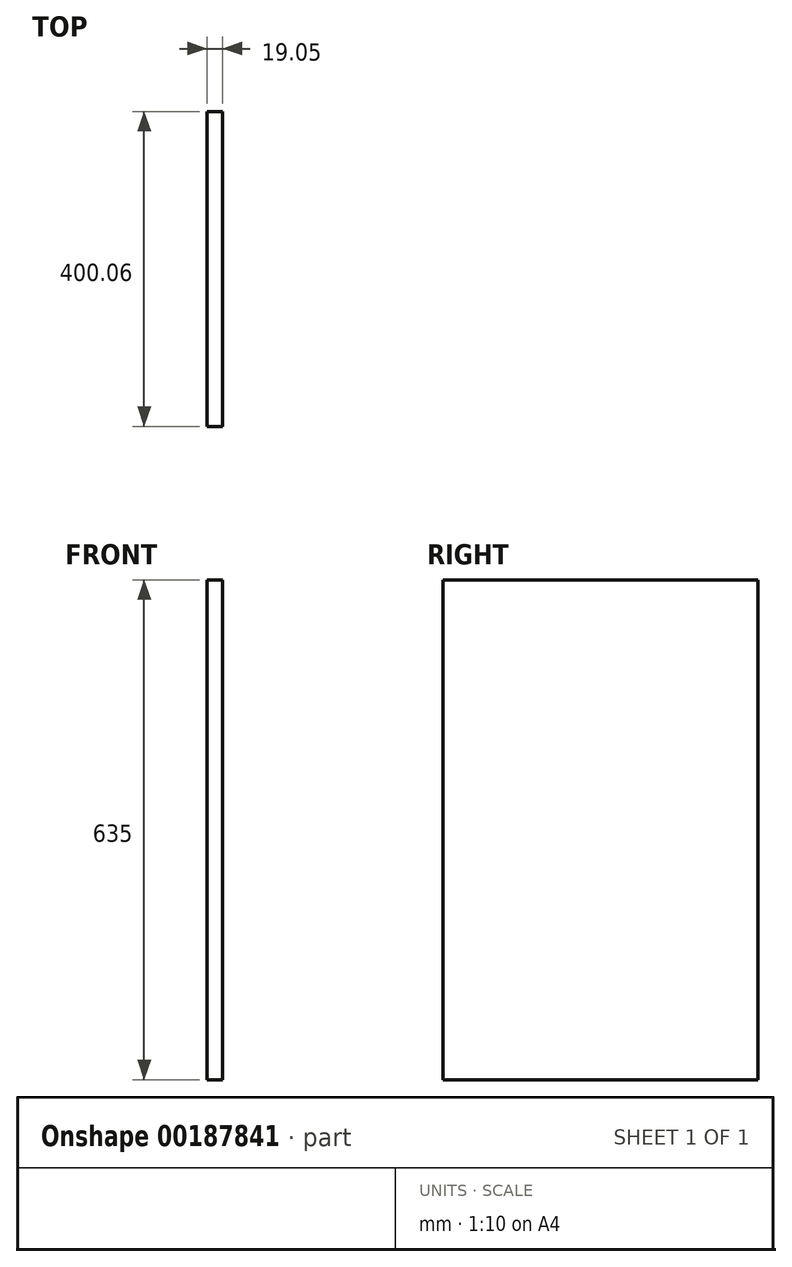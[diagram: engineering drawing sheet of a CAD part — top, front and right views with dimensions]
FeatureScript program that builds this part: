
annotation { "Feature Type Name" : "Feature", "Feature Type Description" : "" }
export const myFeature = defineFeature(function(context is Context, id is Id, definition is map)
    precondition{}
    {
        {
            var Q0;
            Q0=qCreatedBy(makeId("Right.planeOp"),FACE);
            var sketch = newSketch(context, id + "F0", { "sketchPlane" : qUnion([Q0])});
            skLineSegment(sketch, "E0.bottom", {"start": v(-200.02, 317.5) * mm, "end": v(200.03, 317.5) * mm});
            skLineSegment(sketch, "E0.top", {"start": v(-200.03, -317.5) * mm, "end": v(200.02, -317.5) * mm});
            skLineSegment(sketch, "E0.left", {"start": v(-200.02, 317.5) * mm, "end": v(-200.03, -317.5) * mm});
            skLineSegment(sketch, "E0.right", {"start": v(200.03, 317.5) * mm, "end": v(200.02, -317.5) * mm});
            skPoint(sketch, "E0.middle", {"position": v(0, 0) * mm});
            skSolve(sketch);
        }
        {
            var Q0;
            Q0 = qSketchRegion(id + "F0", true);
            extrude(context, id + "F1", {"entities" : qUnion([Q0]), "depth" : 19.05 * mm});
        }
    });
